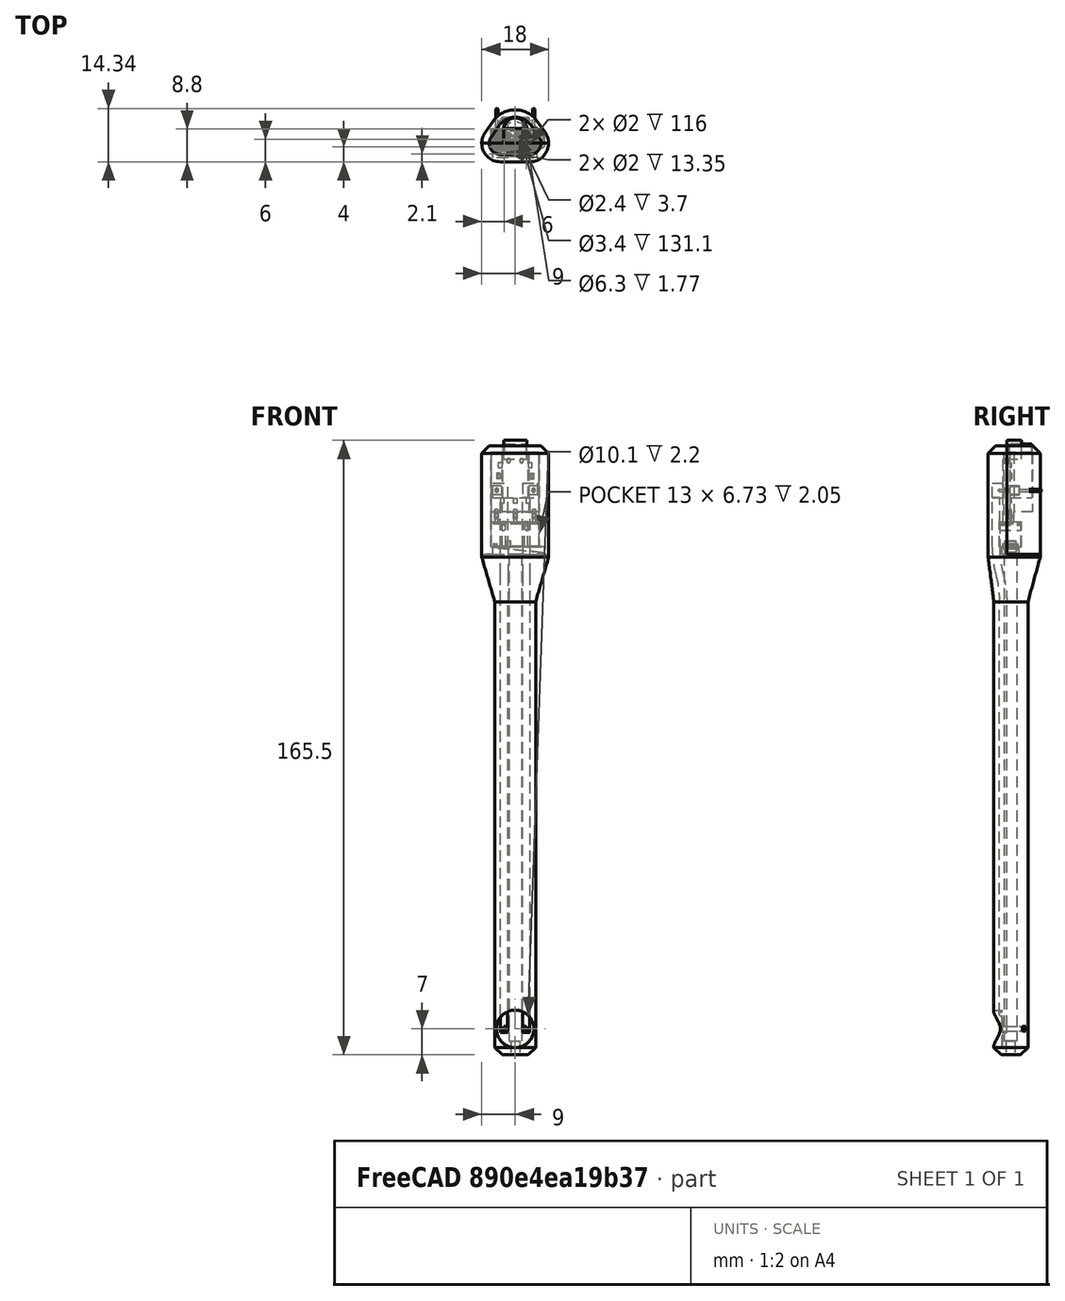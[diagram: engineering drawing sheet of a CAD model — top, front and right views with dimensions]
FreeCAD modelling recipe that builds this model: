
FCSTD DOCUMENT  (FreeCAD 0.16R6712 (Git))
Label: pisakUS_pcb_skorupa
License: All rights reserved
LicenseURL: http://en.wikipedia.org/wiki/All_rights_reserved
objects: Part::Feature×21, Sketcher::SketchObject×6, Part::Box×6, PartDesign::Pad×3, Part::FeaturePython×2, Part::Chamfer×2, Part::Compound×2, Part::MultiFuse×2, Part::Cut×2, Mesh::Feature×2, Part::Loft×1, Part::Fillet×1, Part::Cylinder×1, Part::Sweep×1, Part::Mirroring×1, Part::MultiCommon×1
note: 55 computed .brp shape members not serialized (recipe doc carries the construction recipe); baked Part::Feature solids carry a one-line shape summary decoded from their .brp

FEATURE [Part::FeaturePython] MA40S4S_grubas_01  # a2plus imported part (geometry in sourceFile) (typed FeaturePython)
  Placement = pos=(0,-2.3,-59) rot=(1,0,0;1.5708rad)
  fixedPosition = false
  sourceFile = <path>
  timeLastImport = 1.53199e+09
  updateColors = true
FEATURE [Sketcher::SketchObject] Sketch  label="rurka_krzywa"
  Placement = pos=(3,0,0) rot=(0.57735,0.57735,0.57735;2.0944rad)
  expr: Constraints[19] = Constraints.zakret
  sketch-geometry (7):
    g0: LineSegment StartX=-2 StartY=-60 StartZ=0 EndX=-2 EndY=56 EndZ=0
    g1: LineSegment StartX=-2.94737 StartY=63.34 StartZ=0 EndX=-2.95263 EndY=63.36 EndZ=0
    g2: LineSegment StartX=-3.9 StartY=70.7 StartZ=0 EndX=-3.9 EndY=84.05 EndZ=0
    g3: LineSegment [constr] StartX=-2 StartY=-60 StartZ=0 EndX=0 EndY=-60 EndZ=0
    g4: ArcOfCircle CenterX=25.0078 CenterY=70.7 CenterZ=0 NormalX=0 NormalY=0 NormalZ=1 Radius=28.9078 StartAngle=3.14159 EndAngle=3.39831
    g5: ArcOfCircle CenterX=-30.9078 CenterY=56 CenterZ=0 NormalX=0 NormalY=0 NormalZ=1 Radius=28.9078 StartAngle=0 EndAngle=0.256721
    g6: LineSegment [constr] StartX=0 StartY=70.6298 StartZ=0 EndX=-2.3 EndY=70.6298 EndZ=0
  constraints (20):
    c: Vertical(g0)
    c: Vertical(g2)
    c: DistanceY(g0,g-1) = 60
    c: Coincident(g3,g0)
    c: PointOnObject(g3,g-2)
    c: Horizontal(g3)
    c: DistanceX(g3,g3) = 2
    c: Tangent(g2,g4) = 1.5708
    c: Tangent(g1,g4) = 1.5708
    c: Tangent(g0,g5) = -1.5708
    c: Tangent(g1,g5) = -1.5708
    c: DistanceY(g-1,g0) = 56
    c: DistanceY(g-1,g2) = 70.7
    c: DistanceY(g2,g2) = 13.35
    c: PointOnObject(g6,g-2)
    c: Horizontal(g6)
    c: DistanceX(g6,g6) = 2.3
    c: DistanceX(g2,g6) = 1.6
    c: DistanceY(g1,g2) = 7.34  'zakret'
    c: DistanceY(g0,g1) = 7.34
FEATURE [Sketcher::SketchObject] Sketch001  label="rurka_otwor"
  Placement = pos=(0,0,-60) rot=(0,0,1;0rad)
  sketch-geometry (1):
    g0: Circle CenterX=3 CenterY=-2 CenterZ=0 NormalX=0 NormalY=0 NormalZ=1 Radius=1
  constraints (3):
    c: DistanceY(g0,g-1) = 2
    c: DistanceX(g-1,g0) = 3
    c: Radius(g0) = 1
FEATURE [Part::Box] Box  label="Cube"
  Height = 4
  Length = 4
  Placement = pos=(2,-4.9,84) rot=(0,0,1;0rad)
  Width = 3
FEATURE [Sketcher::SketchObject] Sketch004
  Placement = pos=(0,0,-66) rot=(1,0,0;3.14159rad)
  sketch-geometry (8):
    g0: LineSegment StartX=-2 StartY=4.5 StartZ=0 EndX=2 EndY=4.5 EndZ=0
    g1: LineSegment StartX=4.7021 StartY=-1.22456 StartZ=0 EndX=3.01091 EndY=-3.27879 EndZ=0
    g2: LineSegment StartX=-3.01091 StartY=-3.27879 StartZ=0 EndX=-4.7021 EndY=-1.22456 EndZ=0
    g3: ArcOfCircle CenterX=-2 CenterY=1 CenterZ=0 NormalX=0 NormalY=0 NormalZ=1 Radius=3.5 StartAngle=1.5708 EndAngle=3.83036
    g4: ArcOfCircle CenterX=2 CenterY=1 CenterZ=0 NormalX=0 NormalY=0 NormalZ=1 Radius=3.5 StartAngle=5.59442 EndAngle=7.85398
    g5: ArcOfCircle CenterX=0 CenterY=-0.8 CenterZ=0 NormalX=0 NormalY=0 NormalZ=1 Radius=3.9 StartAngle=3.83036 EndAngle=5.59442
    g6: LineSegment [constr] StartX=-5.5 StartY=1 StartZ=0 EndX=5.5 EndY=1 EndZ=0
    g7: GeomPoint [constr] X=0 Y=-4.7 Z=0
  constraints (20):
    c: Horizontal(g0)
    c: Tangent(g2,g3) = 1.5708
    c: Tangent(g0,g3) = 1.5708
    c: Tangent(g0,g4) = 1.5708
    c: Tangent(g1,g4) = 1.5708
    c: Tangent(g2,g5) = 1.5708
    c: Tangent(g1,g5) = 1.5708
    c: Symmetric(g3,g4,g-2)
    c: DistanceX(g3,g4) = 4
    c: Equal(g1,g2)
    c: DistanceY(g5,g4) = 1.8
    c: DistanceY(g-1,g3) = 1
    c: DistanceY(g3,g0) = 3.5
    c: Horizontal(g6)
    c: PointOnObject(g4,g6)
    c: Symmetric(g6,g6,g-2)
    c: DistanceX(g6,g6) = 11
    c: PointOnObject(g7,g5)
    c: PointOnObject(g7,g-2)
    c: DistanceY(g7,g0) = 9.2
FEATURE [PartDesign::Pad] Pad
  Length = 122
  Length2 = 120
  Placement = pos=(0,0,-66) rot=(1,0,0;3.14159rad)
  Reversed = true
  Sketch = -> Sketch004
  Type = 0
FEATURE [Part::Chamfer] Chamfer  label="trzon"
  Base = -> Pad
  Edges = 6 edges r=2: [Edge3,Edge6,Edge9,Edge12,Edge15,Edge17]
FEATURE [Sketcher::SketchObject] Sketch005  label="gora_trojkat"
  Placement = pos=(0,0,56) rot=(1,0,0;3.14159rad)
  sketch-geometry (8):
    g0: LineSegment StartX=-2 StartY=4.5 StartZ=0 EndX=2 EndY=4.5 EndZ=0
    g1: LineSegment StartX=4.7021 StartY=-1.22456 StartZ=0 EndX=3.01091 EndY=-3.27879 EndZ=0
    g2: LineSegment StartX=-3.01091 StartY=-3.27879 StartZ=0 EndX=-4.7021 EndY=-1.22456 EndZ=0
    g3: ArcOfCircle CenterX=-2 CenterY=1 CenterZ=0 NormalX=0 NormalY=0 NormalZ=1 Radius=3.5 StartAngle=1.5708 EndAngle=3.83036
    g4: ArcOfCircle CenterX=2 CenterY=1 CenterZ=0 NormalX=0 NormalY=0 NormalZ=1 Radius=3.5 StartAngle=5.59442 EndAngle=7.85398
    g5: ArcOfCircle CenterX=0 CenterY=-0.8 CenterZ=0 NormalX=0 NormalY=0 NormalZ=1 Radius=3.9 StartAngle=3.83036 EndAngle=5.59442
    g6: LineSegment [constr] StartX=-5.5 StartY=1 StartZ=0 EndX=5.5 EndY=1 EndZ=0
    g7: GeomPoint [constr] X=0 Y=-4.7 Z=0
  constraints (20):
    c: Horizontal(g0)
    c: Tangent(g2,g3) = 1.5708
    c: Tangent(g0,g3) = 1.5708
    c: Tangent(g0,g4) = 1.5708
    c: Tangent(g1,g4) = 1.5708
    c: Tangent(g2,g5) = 1.5708
    c: Tangent(g1,g5) = 1.5708
    c: Symmetric(g3,g4,g-2)
    c: DistanceX(g3,g4) = 4
    c: Equal(g1,g2)
    c: DistanceY(g5,g4) = 1.8
    c: DistanceY(g-1,g3) = 1
    c: DistanceY(g3,g0) = 3.5
    c: Horizontal(g6)
    c: PointOnObject(g4,g6)
    c: Symmetric(g6,g6,g-2)
    c: DistanceX(g6,g6) = 11
    c: PointOnObject(g7,g5)
    c: PointOnObject(g7,g-2)
    c: DistanceY(g7,g0) = 9.2
FEATURE [Sketcher::SketchObject] Sketch006  label="glowka"
  Placement = pos=(0,0,68) rot=(1,0,0;3.14159rad)
  sketch-geometry (8):
    g0: LineSegment StartX=-4 StartY=6 StartZ=0 EndX=4 EndY=6 EndZ=0
    g1: LineSegment StartX=8.06199 StartY=-1.91552 StartZ=0 EndX=5.84926 EndY=-4.99835 EndZ=0
    g2: LineSegment StartX=-5.84926 StartY=-4.99835 StartZ=0 EndX=-8.06199 EndY=-1.91552 EndZ=0
    g3: ArcOfCircle CenterX=-4 CenterY=1 CenterZ=0 NormalX=0 NormalY=0 NormalZ=1 Radius=5 StartAngle=1.5708 EndAngle=3.76414
    g4: ArcOfCircle CenterX=4 CenterY=1 CenterZ=0 NormalX=0 NormalY=0 NormalZ=1 Radius=5 StartAngle=5.66064 EndAngle=7.85398
    g5: ArcOfCircle CenterX=0 CenterY=-0.8 CenterZ=0 NormalX=0 NormalY=0 NormalZ=1 Radius=7.2 StartAngle=3.76414 EndAngle=5.66064
    g6: LineSegment [constr] StartX=-5.5 StartY=1 StartZ=0 EndX=5.5 EndY=1 EndZ=0
    g7: GeomPoint [constr] X=0 Y=-8 Z=0
  constraints (20):
    c: Horizontal(g0)
    c: Tangent(g2,g3) = 1.5708
    c: Tangent(g0,g3) = 1.5708
    c: Tangent(g0,g4) = 1.5708
    c: Tangent(g1,g4) = 1.5708
    c: Tangent(g2,g5) = 1.5708
    c: Tangent(g1,g5) = 1.5708
    c: Symmetric(g3,g4,g-2)
    c: DistanceX(g3,g4) = 8
    c: Equal(g1,g2)
    c: DistanceY(g5,g4) = 1.8
    c: DistanceY(g-1,g3) = 1
    c: DistanceY(g3,g0) = 5
    c: Horizontal(g6)
    c: PointOnObject(g4,g6)
    c: Symmetric(g6,g6,g-2)
    c: DistanceX(g6,g6) = 11
    c: PointOnObject(g7,g5)
    c: PointOnObject(g7,g-2)
    c: DistanceY(g7,g0) = 14
FEATURE [PartDesign::Pad] Pad001  label="glowka001"
  Length = 30
  Length2 = 100
  Placement = pos=(0,0,68) rot=(1,0,0;3.14159rad)
  Reversed = true
  Sketch = -> Sketch006
  Type = 0
FEATURE [Part::Loft] Loft
  Closed = false
  Ruled = false
  Sections = -> [Sketch006,Sketch005]
  Solid = true
FEATURE [Part::Chamfer] Chamfer001  label="glowka002"
  Base = -> Pad001
  Edges = 6 edges r=2: [Edge4,Edge7,Edge10,Edge13,Edge16,Edge18]
FEATURE [Part::Feature] Part__Feature018  label="SOLID004"
  Placement = pos=(4.572,-8.636,1.65) rot=(0,0,-1;1.5708rad)
  shape: bbox 0.85 x 1.55 x 0.45 mm, 28 faces (baked)
FEATURE [Part::Feature] Part__Feature019  label="COMPOUND013"
  Placement = pos=(-3.25,-22.582,-1.05) rot=(0,0,1;3.14159rad)
  shape: bbox 13.03 x 2.3 x 3.8 mm, 9 faces (baked)
FEATURE [Part::Feature] Part__Feature020  label="COMPOUND014"
  Placement = pos=(-3.25,-22.582,-1.05) rot=(0,0,1;3.14159rad)
  shape: bbox 12.8 x 10 x 5.8 mm, 68 faces (baked)
FEATURE [Part::Feature] Part__Feature021  label="COMPOUND015"
  Placement = pos=(-3.25,-22.582,-1.05) rot=(0,0,1;3.14159rad)
  shape: bbox 1.2 x 2 x 2.9 mm, 6 faces (baked)
FEATURE [Part::Feature] Part__Feature022  label="LED_0604"
  Placement = pos=(-2.54,-18.796,1.65) rot=(0,0,-1;1.5708rad)
FEATURE [Part::Feature] Part__Feature023  label="COMPOUND016"
  Placement = pos=(0,0,1.65) rot=(0,0,1;0rad)
  shape: bbox 7 x 12 x 6 mm, 6 faces (baked)
FEATURE [Part::Feature] Part__Feature024  label="COMPOUND017"
  Placement = pos=(0,0,1.65) rot=(0,0,1;0rad)
  shape: bbox 1 x 1 x 1.1 mm, 3 faces (baked)
FEATURE [Part::Feature] Part__Feature025  label="COMPOUND018"
  Placement = pos=(0,0,1.65) rot=(0,0,1;0rad)
  shape: bbox 1 x 1 x 1.1 mm, 3 faces (baked)
FEATURE [Part::Feature] Part__Feature026  label="COMPOUND019"
  Placement = pos=(0,0,1.65) rot=(0,0,1;0rad)
  shape: bbox 1.2 x 1.05 x 0.4 mm, 6 faces (baked)
FEATURE [Part::Feature] Part__Feature027  label="COMPOUND020"
  Placement = pos=(0,0,1.65) rot=(0,0,1;0rad)
  shape: bbox 1.05 x 1.2 x 0.4 mm, 6 faces (baked)
FEATURE [Part::Feature] Part__Feature028  label="COMPOUND021"
  Placement = pos=(0,0,1.65) rot=(0,0,1;0rad)
  shape: bbox 1.05 x 1.2 x 0.4 mm, 6 faces (baked)
FEATURE [Part::Feature] Part__Feature029  label="COMPOUND022"
  Placement = pos=(0,0,1.65) rot=(0,0,1;0rad)
  shape: bbox 1.05 x 1.2 x 0.4 mm, 6 faces (baked)
FEATURE [Part::Feature] Part__Feature030  label="COMPOUND023"
  Placement = pos=(0,0,1.65) rot=(0,0,1;0rad)
  shape: bbox 1.05 x 1.2 x 0.4 mm, 6 faces (baked)
FEATURE [Part::Feature] Part__Feature031  label="COMPOUND024"
  Placement = pos=(0,0,1.65) rot=(0,0,1;0rad)
  shape: bbox 6 x 2.5 x 6 mm, 3 faces (baked)
FEATURE [Part::Feature] Part__Feature032  label="SOLID005"
  Placement = pos=(-4.572,-8.636,1.65) rot=(0,0,1;1.5708rad)
  shape: bbox 0.85 x 1.55 x 0.45 mm, 28 faces (baked)
FEATURE [Part::Feature] Part__Feature033  label="SOLID006"
  Placement = pos=(4.953,-12.446,1.65) rot=(0,0,1;0rad)
  shape: bbox 2.54 x 2.54 x 11.54 mm, 28 faces (baked)
FEATURE [Part::Feature] Part__Feature034  label="SOLID007"
  Placement = pos=(-4.953,-12.446,1.65) rot=(0,0,1;0rad)
  shape: bbox 2.54 x 2.54 x 11.54 mm, 28 faces (baked)
FEATURE [Part::Feature] Part__Feature035  label="COMPOUND025"
  shape: bbox 12.7 x 18.67 x 1.6 mm, 10 faces (baked)
FEATURE [Part::Compound] Compound001  label="pisakUS_pcb3"
  Links = -> [Part__Feature018,Part__Feature033,Part__Feature034,Part__Feature035,Part__Feature022,Part__Feature023,Part__Feature025,Part__Feature024,Part__Feature026,Part__Feature028,Part__Feature030,Part__Feature031,Part__Feature027,Part__Feature029,Part__Feature032,Part__Feature020,Part__Feature021,Part__Feature019]
  Placement = pos=(0,-1.85,98.5) rot=(0,0.707107,0.707107;3.14159rad)
FEATURE [Part::Box] Box001  label="wyciecie_przycisk1"
  Height = 6.73
  Length = 13
  Placement = pos=(-6.5,-3,70.8) rot=(0,0,1;0rad)
  Width = 6
FEATURE [Part::Box] Box002  label="wyciecie_przycisk2"
  Height = 2
  Length = 14
  Placement = pos=(-6,-2.3,68.8) rot=(0,0,1;0rad)
  Width = 4.6
FEATURE [Part::Fillet] Fillet  label="wyciecie_przycisk003"
  Base = -> Box002
  Edges = 2 edges r=1: [Edge5,Edge7]
FEATURE [Part::Box] Box003  label="wyciecie_pcb1"
  Height = 18.7
  Length = 13
  Placement = pos=(-6.5,-2,77.53) rot=(0,0,1;0rad)
  Width = 2.95
FEATURE [Part::Cylinder] Cylinder  label="wyciecie_jack"
  Angle = 360
  Height = 10
  Placement = pos=(0,2.8,96) rot=(0,0,1;0rad)
  Radius = 3.15
FEATURE [Sketcher::SketchObject] Sketch007  label="glowka_wyciecie4"
  Placement = pos=(0,0,96.23) rot=(1,0,0;3.14159rad)
  sketch-geometry (4):
    g0: LineSegment StartX=-6.5 StartY=-0.95 StartZ=0 EndX=6.5 EndY=-0.95 EndZ=0
    g1: LineSegment StartX=6.5 StartY=-0.95 StartZ=0 EndX=3.6 EndY=-5.95 EndZ=0
    g2: LineSegment StartX=3.6 StartY=-5.95 StartZ=0 EndX=-3.6 EndY=-5.95 EndZ=0
    g3: LineSegment StartX=-3.6 StartY=-5.95 StartZ=0 EndX=-6.5 EndY=-0.95 EndZ=0
  constraints (12):
    c: Horizontal(g0)
    c: Coincident(g0,g1)
    c: Coincident(g1,g2)
    c: Horizontal(g2)
    c: Coincident(g2,g3)
    c: Coincident(g0,g3)
    c: Symmetric(g0,g0,g-2)
    c: Symmetric(g2,g1,g-2)
    c: DistanceY(g0,g-1) = 0.95
    c: DistanceY(g2,g0) = 5
    c: DistanceX(g0,g0) = 13
    c: DistanceX(g2,g2) = 7.2
FEATURE [PartDesign::Pad] Pad002  label="wyciecie4"
  Length = 16
  Length2 = 100
  Placement = pos=(0,0,96.23) rot=(1,0,0;3.14159rad)
  Sketch = -> Sketch007
  Type = 0
FEATURE [Part::MultiFuse] Fusion001  label="skorupa_pisakUS"
  Shapes = -> [Chamfer,Loft,Chamfer001]
FEATURE [Part::Box] Box006  label="wyciecie_glowka_gora1"
  Height = 31
  Length = 24
  Placement = pos=(-12,-1,68.8) rot=(0,0,1;0rad)
  Width = 12
FEATURE [Part::Box] Box006002  label="wyciecie_jack001"
  Height = 5
  Length = 6.28
  Placement = pos=(-3.126,-1,94.5) rot=(0,0,1;0rad)
  Width = 4
FEATURE [Part::Feature] Box006002001  label="wyciecie_jack002"
  Placement = pos=(-3.126,-1,94.5) rot=(0,0,1;0rad)
  shape: bbox 6.28 x 4 x 5 mm, 6 faces (baked)
FEATURE [Part::FeaturePython] wklad_34_01  # a2plus imported part (geometry in sourceFile) (typed FeaturePython)
  Placement = pos=(0,0,0) rot=(1,0,0;1.5708rad)
  fixedPosition = false
  sourceFile = <path>
  timeLastImport = 1.53233e+09
  updateColors = true
FEATURE [Part::Sweep] Sweep
  Frenet = false
  Sections = -> [Sketch001]
  Solid = true
  Spine = -> Sketch [Edge5,Edge4,Edge3,Edge2,Edge1]
  Transition = 1
FEATURE [Part::Compound] Compound  label="przewody"
  Links = -> [Sweep,Box]
FEATURE [Part::Mirroring] Part__Mirroring  label="przewody (Mirror #1)"
  Base = (0,0,0)
  Normal = (1,0,0)
  Source = -> Compound
FEATURE [Part::MultiFuse] Fusion  label="wnetrze"
  Shapes = -> [Part__Mirroring,wklad_34_01,Box001,Box003,Cylinder,Fillet,MA40S4S_grubas_01,Pad002,Compound]
FEATURE [Part::Feature] Box006002002  label="wyciecie_glowka_gora002"
  Placement = pos=(-12,-1,68.8) rot=(0,0,1;0rad)
  shape: bbox 24 x 12 x 31 mm, 6 faces (baked)
FEATURE [Part::Cut] Cut  label="pisak"
  Base = -> Fusion001
  Tool = -> Fusion
FEATURE [Part::Feature] Cut001  label="pisak001"
  shape: bbox 18.64 x 14.37 x 164 mm, 100 faces (baked)
FEATURE [Part::MultiCommon] Common  label="gora"
  Shapes = -> [Cut001,Box006002002]
FEATURE [Part::Cut] Cut002  label="dol"
  Base = -> Cut
  Tool = -> Box006
FEATURE [Mesh::Feature] Mesh  label="gora (Meshed)"
FEATURE [Mesh::Feature] Mesh001  label="dol (Meshed)"
note: 2 file-system paths scrubbed to <path> (originals preserved in the JSON sidecar)
